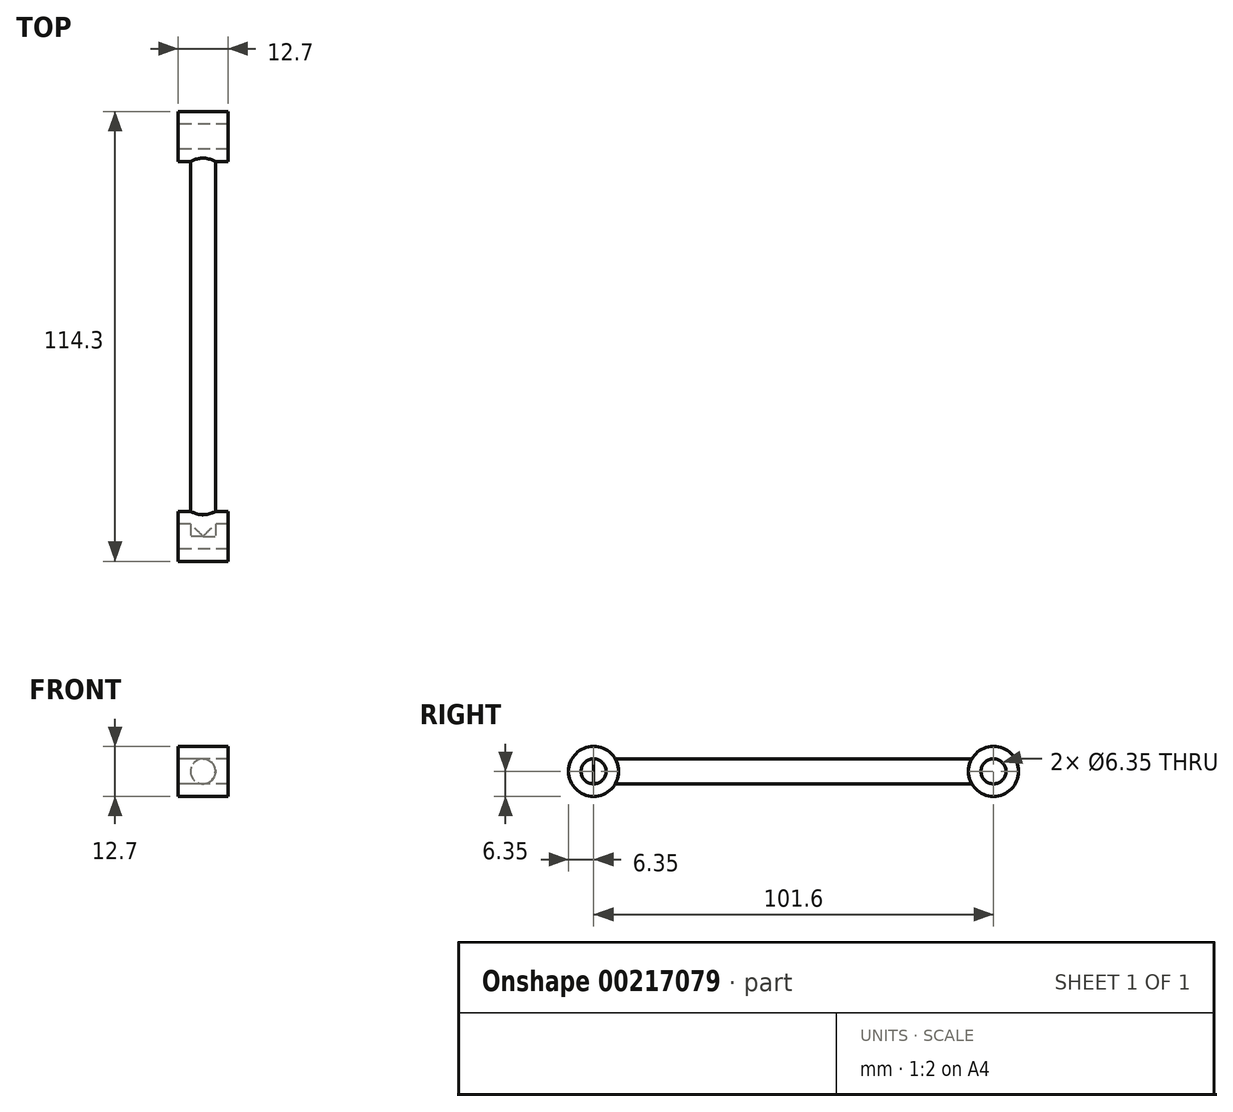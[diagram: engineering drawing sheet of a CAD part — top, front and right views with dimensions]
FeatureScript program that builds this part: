
annotation { "Feature Type Name" : "Feature", "Feature Type Description" : "" }
export const myFeature = defineFeature(function(context is Context, id is Id, definition is map)
    precondition{}
    {
        {
            var Q0;
            Q0=qCreatedBy(makeId("Right.planeOp"),FACE);
            var sketch = newSketch(context, id + "F0", { "sketchPlane" : qUnion([Q0])});
            skCircle(sketch, "E0", {"center": v(0, 0) * mm, "radius": 3.18 * mm});
            skLineSegment(sketch, "E1", {"start": v(0, 0) * mm, "end": v(101.6, 0) * mm, "construction": true});
            skCircle(sketch, "E2", {"center": v(101.6, 0) * mm, "radius": 3.18 * mm});
            skCircle(sketch, "E3", {"center": v(0, 0) * mm, "radius": 6.35 * mm});
            skCircle(sketch, "E4", {"center": v(101.6, 0) * mm, "radius": 6.35 * mm});
            skSolve(sketch);
        }
        {
            var Q0;
            Q0=qCreatedBy(makeId("Front.planeOp"),FACE);
            var sketch = newSketch(context, id + "F1", { "sketchPlane" : qUnion([Q0])});
            skCircle(sketch, "E5", {"center": v(0, 0) * mm, "radius": 3.18 * mm});
            skSolve(sketch);
        }
        {
            var Q0;
            Q0 = qSketchRegion(id + "F0", true);
            extrude(context, id + "F2", {"entities" : qUnion([Q0]), "depth" : 12.7 * mm, "symmetric" : true});
        }
        {
            var Q0;
            Q0 = qSketchRegion(id + "F1", true);
            var Q1;
            Q1=makeQuery(id+"F2.opExtrude","SWEPT_FACE",FACE,{"disambiguationData":[OSD([sQuery(id+"F0.wireOp",EDGE,"E4")])]});
            extrude(context, id + "F3", {"entities" : qUnion([Q0]), "operationType" : NewBodyOperationType.ADD, "endBound" : BoundingType.UP_TO_SURFACE, "oppositeDirection" : true, "endBoundEntityFace" : qUnion([Q1]), "depth" : 25.4 * mm});
        }
    });
